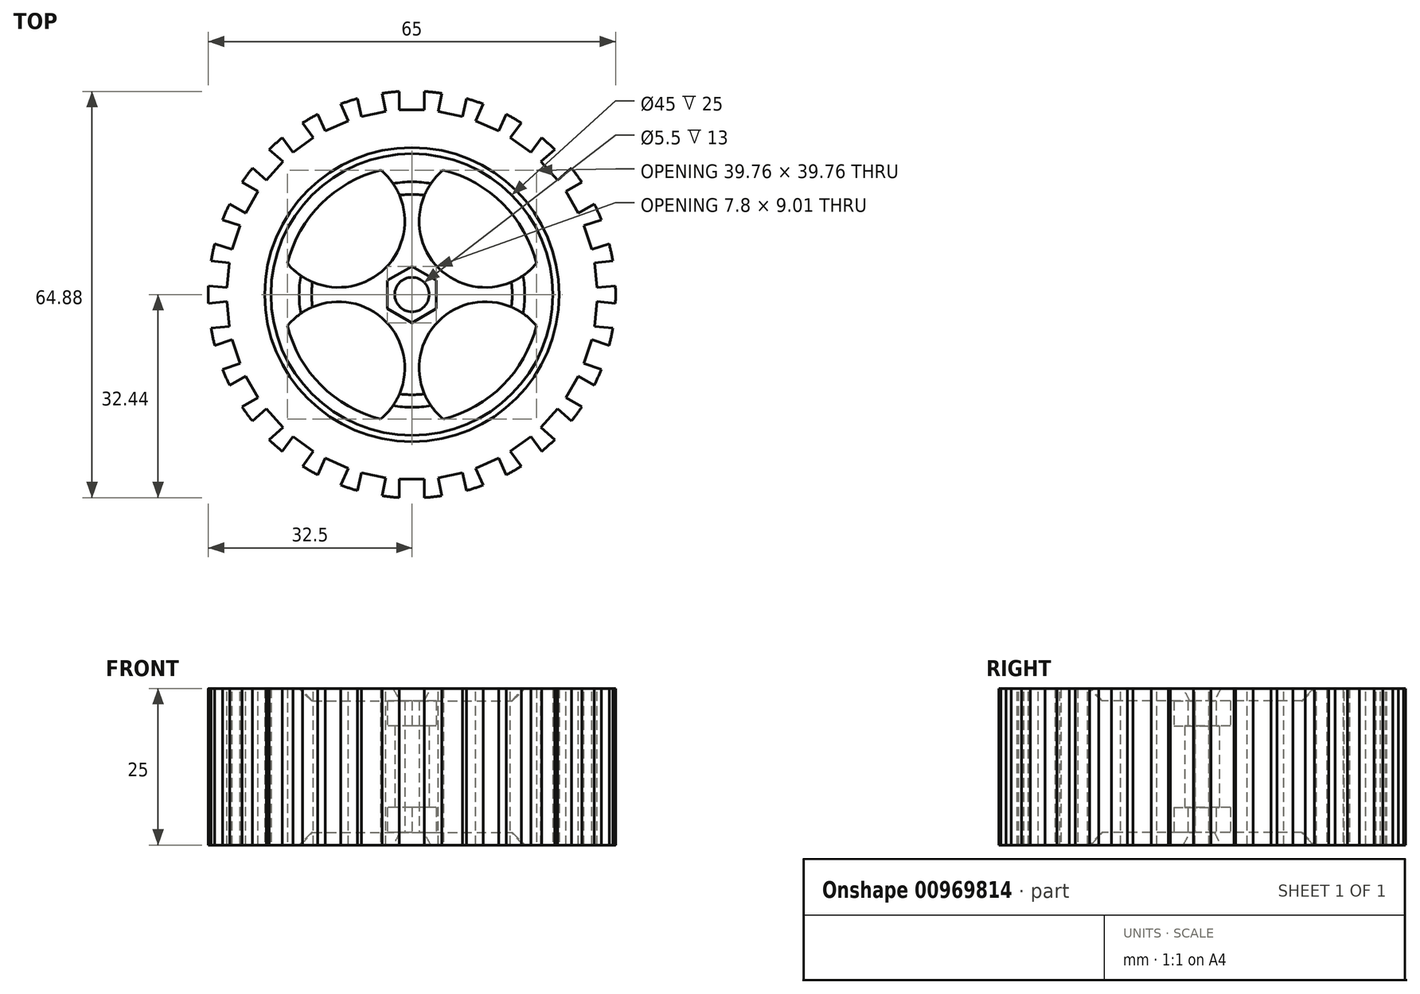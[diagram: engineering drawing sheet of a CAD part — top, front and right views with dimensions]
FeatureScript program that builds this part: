
annotation { "Feature Type Name" : "Feature", "Feature Type Description" : "" }
export const myFeature = defineFeature(function(context is Context, id is Id, definition is map)
    precondition{}
    {
        {
            assignVariable(context, id + "F0", {"name" : "Height", "anyValue" : 25});
        }
        {
            assignVariable(context, id + "F1", {"name" : "TreadCount", "anyValue" : 30});
        }
        {
            assignVariable(context, id + "F2", {"name" : "WheelDiameter", "anyValue" : 65});
        }
        {
            assignVariable(context, id + "F3", {"name" : "TireThickness", "anyValue" : 10});
        }
        {
            var Q0;
            Q0=qCreatedBy(makeId("Top.planeOp"),FACE);
            var sketch = newSketch(context, id + "F4", { "sketchPlane" : qUnion([Q0])});
            skCircle(sketch, "E0", {"center": v(0, 0) * mm, "radius": 32.5 * mm});
            skCircle(sketch, "E1", {"center": v(0, 0) * mm, "radius": 22.5 * mm});
            skCircle(sketch, "E2", {"center": v(0, 0) * mm, "radius": 2.75 * mm});
            skCircle(sketch, "E3", {"center": v(0, 0) * mm, "radius": 6 * mm});
            skCircle(sketch, "E4", {"center": v(0, 0) * mm, "radius": 23.5 * mm});
            skCircle(sketch, "E5", {"center": v(0, 0) * mm, "radius": 20.5 * mm});
            skArc(sketch, "E6", {"start": v(-19.88, 5) * mm, "mid": v(-4.24, 4.24) * mm, "end": v(-5, 19.88) * mm});
            skArc(sketch, "E7.MirrorCS", {"start": v(19.88, 5) * mm, "mid": v(4.24, 4.24) * mm, "end": v(5, 19.88) * mm});
            skArc(sketch, "E8.MirrorCS", {"start": v(19.88, -5) * mm, "mid": v(4.24, -4.24) * mm, "end": v(5, -19.88) * mm});
            skArc(sketch, "E9.MirrorCS", {"start": v(-19.88, -5) * mm, "mid": v(-4.24, -4.24) * mm, "end": v(-5, -19.88) * mm});
            skCircle(sketch, "E10.cCircle", {"center": v(0, 0) * mm, "radius": 3.9 * mm, "construction": true});
            skLineSegment(sketch, "E10.0", {"start": v(-3.9, -2.25) * mm, "end": v(-3.9, 2.25) * mm});
            skLineSegment(sketch, "E10.1", {"start": v(-3.9, 2.25) * mm, "end": v(0, 4.5) * mm});
            skLineSegment(sketch, "E10.2", {"start": v(0, 4.5) * mm, "end": v(3.9, 2.25) * mm});
            skLineSegment(sketch, "E10.3", {"start": v(3.9, 2.25) * mm, "end": v(3.9, -2.25) * mm});
            skLineSegment(sketch, "E10.4", {"start": v(3.9, -2.25) * mm, "end": v(0, -4.5) * mm});
            skLineSegment(sketch, "E10.5", {"start": v(0, -4.5) * mm, "end": v(-3.9, -2.25) * mm});
            skPoint(sketch, "E10.0.midPoint", {"position": v(-3.9, 0) * mm});
            skCircle(sketch, "E11", {"center": v(0, 0) * mm, "radius": 3 * mm});
            skSolve(sketch);
        }
        {
            var Q0;
            {var subQ0=sQuery(id+"F4.wireOp",EDGE,"E6");var subQ1=sQuery(id+"F4.wireOp",EDGE,"E3");var subQ2=makeQuery(id+"F4.imprint","INTERSECT",VERTEX,{"derivedFrom":[subQ1,subQ0]});Q0=makeQuery(id+"F4.imprint","IMPRINT",FACE,{"disambiguationData":[TD([[makeQuery(id+"F4.imprint","IMPRINT",EDGE,{"disambiguationData":[TD([[subQ2,-1.0]])],"derivedFrom":subQ1}),-1.0]])]});}
            var Q1;
            Q1=makeQuery(id+"F4.imprint","IMPRINT",FACE,{"disambiguationData":[TD([[makeQuery(id+"F4.imprint","IMPRINT",EDGE,{"derivedFrom":sQuery(id+"F4.wireOp",EDGE,"E1")}),1.0]])]});
            var Q2;
            Q2=makeQuery(id+"F4.imprint","IMPRINT",FACE,{"disambiguationData":[TD([[makeQuery(id+"F4.imprint","IMPRINT",EDGE,{"derivedFrom":sQuery(id+"F4.wireOp",EDGE,"E1")}),-1.0]])]});
            var Q3;
            {var subQ0=sQuery(id+"F4.wireOp",EDGE,"E6");var subQ1=sQuery(id+"F4.wireOp",EDGE,"E3");var subQ2=makeQuery(id+"F4.imprint","INTERSECT",VERTEX,{"derivedFrom":[subQ1,subQ0]});Q3=makeQuery(id+"F4.imprint","IMPRINT",FACE,{"disambiguationData":[TD([[makeQuery(id+"F4.imprint","IMPRINT",EDGE,{"disambiguationData":[TD([[subQ2,1.0]])],"derivedFrom":subQ1}),-1.0]])]});}
            var Q4;
            {var subQ0=sQuery(id+"F4.wireOp",EDGE,"E7.MirrorCS");var subQ1=sQuery(id+"F4.wireOp",EDGE,"E3");var subQ2=makeQuery(id+"F4.imprint","INTERSECT",VERTEX,{"derivedFrom":[subQ1,subQ0]});Q4=makeQuery(id+"F4.imprint","IMPRINT",FACE,{"disambiguationData":[TD([[makeQuery(id+"F4.imprint","IMPRINT",EDGE,{"disambiguationData":[TD([[subQ2,1.0]])],"derivedFrom":subQ1}),-1.0]])]});}
            var Q5;
            Q5=makeQuery(id+"F4.imprint","IMPRINT",FACE,{"disambiguationData":[TD([[makeQuery(id+"F4.imprint","IMPRINT",EDGE,{"derivedFrom":sQuery(id+"F4.wireOp",EDGE,"E10.0")}),1.0]])]});
            var Q6;
            {var subQ0=sQuery(id+"F4.wireOp",EDGE,"E9.MirrorCS");var subQ1=sQuery(id+"F4.wireOp",EDGE,"E3");var subQ2=makeQuery(id+"F4.imprint","INTERSECT",VERTEX,{"derivedFrom":[subQ1,subQ0]});Q6=makeQuery(id+"F4.imprint","IMPRINT",FACE,{"disambiguationData":[TD([[makeQuery(id+"F4.imprint","IMPRINT",EDGE,{"disambiguationData":[TD([[subQ2,-1.0]])],"derivedFrom":subQ1}),-1.0]])]});}
            var Q7;
            Q7=makeQuery(id+"F4.imprint","IMPRINT",FACE,{"disambiguationData":[TD([[makeQuery(id+"F4.imprint","IMPRINT",EDGE,{"derivedFrom":sQuery(id+"F4.wireOp",EDGE,"E10.0")}),-1.0]])]});
            extrude(context, id + "F5", {"entities" : qUnion([Q0, Q1, Q2, Q3, Q4, Q5, Q6, Q7]), "depth" : (getVariable(context, 'Height')) * mm, "offsetDistance" : 25 * mm});
        }
        {
            var Q0;
            Q0=makeQuery(id+"F4.imprint","IMPRINT",FACE,{"disambiguationData":[TD([[makeQuery(id+"F4.imprint","IMPRINT",EDGE,{"derivedFrom":sQuery(id+"F4.wireOp",EDGE,"E0")}),1.0]])]});
            var Q1;
            Q1=makeQuery(id+"F4.imprint","IMPRINT",FACE,{"disambiguationData":[TD([[makeQuery(id+"F4.imprint","IMPRINT",EDGE,{"derivedFrom":sQuery(id+"F4.wireOp",EDGE,"E1")}),-1.0]])]});
            extrude(context, id + "F6", {"entities" : qUnion([Q0, Q1]), "depth" : (getVariable(context, 'Height')) * mm, "offsetDistance" : 25 * mm});
        }
        {
            var Q0;
            Q0=makeQuery(id+"F4.imprint","IMPRINT",FACE,{"disambiguationData":[TD([[makeQuery(id+"F4.imprint","IMPRINT",EDGE,{"derivedFrom":sQuery(id+"F4.wireOp",EDGE,"E2")}),-1.0]])]});
            extrude(context, id + "F7", {"entities" : qUnion([Q0]), "operationType" : NewBodyOperationType.ADD, "depth" : (getVariable(context, 'Height') - 2) * mm, "offsetDistance" : 25 * mm, "hasSecondDirection" : true, "secondDirectionOppositeDirection" : false, "secondDirectionDepth" : 2 * mm});
        }
        {
            var Q0;
            Q0=makeQuery(id+"F5.opExtrude","CAP_EDGE",EDGE,{"disambiguationData":[OSD([sQuery(id+"F4.wireOp",EDGE,"E11")])],"isStart":true});
            var Q1;
            Q1=makeQuery(id+"F5.opExtrude","CAP_EDGE",EDGE,{"disambiguationData":[OSD([sQuery(id+"F4.wireOp",EDGE,"E11")])],"isStart":false});
            chamfer(context, id + "F8", {"entities" : qUnion([Q0, Q1]), "width" : 15 * mm, "tangentPropagation" : true});
        }
        {
            var Q0;
            Q0=qCreatedBy(makeId("Front.planeOp"),FACE);
            cPlane(context, id + "F9", {"entities" : qUnion([Q0]), "cplaneType" : CPlaneType.OFFSET, "offset" : (getVariable(context, 'WheelDiameter') / 2) * mm, "width" : 150 * mm, "height" : 150 * mm});
        }
        {
            var Q0;
            Q0=qCreatedBy(id+"F9.planeOp",FACE);
            var sketch = newSketch(context, id + "F10", { "sketchPlane" : qUnion([Q0])});
            skLineSegment(sketch, "E12.bottom", {"start": v(-2, 0) * mm, "end": v(2, 0) * mm});
            skLineSegment(sketch, "E12.top", {"start": v(-2, 25) * mm, "end": v(2, 25) * mm});
            skLineSegment(sketch, "E12.left", {"start": v(-2, 0) * mm, "end": v(-2, 25) * mm});
            skLineSegment(sketch, "E12.right", {"start": v(2, 0) * mm, "end": v(2, 25) * mm});
            skSolve(sketch);
        }
        {
            var Q0;
            Q0=makeQuery(id+"F10.imprint","IMPRINT",FACE,{"disambiguationData":[TD([[makeQuery(id+"F10.imprint","IMPRINT",EDGE,{"derivedFrom":sQuery(id+"F10.wireOp",EDGE,"E12.bottom")}),1.0]])]});
            var Q1;
            Q1=makeQuery(id+"F5.opExtrude","SWEPT_FACE",FACE,{"disambiguationData":[OSD([sQuery(id+"F4.wireOp",EDGE,"E4")])]});
            extrude(context, id + "F11", {"entities" : qUnion([Q0]), "oppositeDirection" : true, "depth" : 3 * mm, "endBoundEntityFace" : qUnion([Q1]), "hasOffset" : true, "offsetDistance" : (getVariable(context, 'TireThickness') - 3) * mm});
        }
        {
            var Q0;
            Q0=makeQuery(id+"F11.opExtrude","SWEPT_BODY",BODY,{"disambiguationData":[OSD([sQuery(id+"F10.wireOp",EDGE,"E12.bottom"),sQuery(id+"F10.wireOp",EDGE,"E12.top"),sQuery(id+"F10.wireOp",EDGE,"E12.left"),sQuery(id+"F10.wireOp",EDGE,"E12.right")])]});
            var Q1;
            Q1=makeQuery(id+"F7.opExtrude","CAP_EDGE",EDGE,{"disambiguationData":[OSD([sQuery(id+"F4.wireOp",EDGE,"E2")])],"isStart":false});
            circularPattern(context, id + "F12", {"operationType" : NewBodyOperationType.REMOVE, "entities" : qUnion([Q0]), "axis" : qUnion([Q1]), "angle" : 360 * degree, "instanceCount" : getVariable(context, 'TreadCount'), "equalSpace" : true});
        }
        {
            var Q0;
            Q0=makeQuery(id+"F4.imprint","IMPRINT",FACE,{"disambiguationData":[TD([[makeQuery(id+"F4.imprint","IMPRINT",EDGE,{"derivedFrom":sQuery(id+"F4.wireOp",EDGE,"E10.0")}),-1.0]])]});
            var Q1;
            Q1=makeQuery(id+"F4.imprint","IMPRINT",FACE,{"disambiguationData":[TD([[makeQuery(id+"F4.imprint","IMPRINT",EDGE,{"derivedFrom":sQuery(id+"F4.wireOp",EDGE,"E2")}),-1.0]])]});
            var Q2;
            Q2=makeQuery(id+"F4.imprint","IMPRINT",FACE,{"disambiguationData":[TD([[makeQuery(id+"F4.imprint","IMPRINT",EDGE,{"derivedFrom":sQuery(id+"F4.wireOp",EDGE,"E2")}),1.0]])]});
            extrude(context, id + "F13", {"entities" : qUnion([Q0, Q1, Q2]), "operationType" : NewBodyOperationType.REMOVE, "depth" : 6 * mm, "offsetDistance" : 25 * mm});
        }
        {
            var Q0;
            Q0=makeQuery(id+"F4.imprint","IMPRINT",FACE,{"disambiguationData":[TD([[makeQuery(id+"F4.imprint","IMPRINT",EDGE,{"derivedFrom":sQuery(id+"F4.wireOp",EDGE,"E10.0")}),-1.0]])]});
            var Q1;
            Q1=makeQuery(id+"F4.imprint","IMPRINT",FACE,{"disambiguationData":[TD([[makeQuery(id+"F4.imprint","IMPRINT",EDGE,{"derivedFrom":sQuery(id+"F4.wireOp",EDGE,"E2")}),-1.0]])]});
            extrude(context, id + "F14", {"entities" : qUnion([Q0, Q1]), "operationType" : NewBodyOperationType.REMOVE, "depth" : (getVariable(context, 'Height')) * mm, "offsetDistance" : 25 * mm, "hasSecondDirection" : true, "secondDirectionOppositeDirection" : false, "secondDirectionDepth" : (getVariable(context, 'Height') - 6) * mm});
        }
    });
